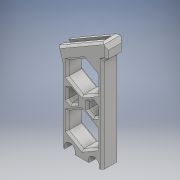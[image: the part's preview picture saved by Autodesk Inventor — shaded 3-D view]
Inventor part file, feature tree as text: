
AUTODESK INVENTOR PART (.ipt)
format: ipt  version: 2018 (Build 220112000, 112)  size: 381,440 bytes
history: native  units: mm
features: extrude x7, sketch x7, fillet x2, plane x1, chamfer x1, projected_geometry x1
ambient origin geometry x8: Origin, YZ Plane, XZ Plane, XY Plane, X Axis, Y Axis, Z Axis, Center Point
bodies: Solid1 (feature_tree)
feature tree (19):
  extrude  "Extrusion1"  Depth=70.0mm
  extrude  "Extrusion2"  Depth=10.0mm
  extrude  "Extrusion3"  TaperAngle=30.0deg  [1 undecoded]
  sketch  "Sketch7"  dims[d12=60.0deg d13=4.0mm d14=5.0mm d15=5.0mm]
  extrude  "Extrusion7"  Depth=5.0mm
  extrude  "Extrusion4"  Depth=7.0mm
  extrude  "Extrusion5"  Depth=4.0mm
  fillet  "Fillet1"  Radius=5.0mm
  fillet  "Fillet2"  Radius=5.0mm
  plane  "Work Plane1"
  extrude  "Extrusion9"  Depth=10.0mm
  chamfer  "Chamfer1"  Distance=15.0mm
  sketch  "Sketch1"  dims[d0=45.0mm d1=70.0mm]
  sketch  "Sketch2"  dims[d2=2.0mm d3=10.0mm]
  sketch  "Sketch3"  dims[d4=11.0mm d6=30.0deg]
  projected_geometry  "Projected Loop1"
  sketch  "Sketch5"  dims[d7=15.0mm d8=0.0mm d9=5.0mm]
  sketch  "Sketch6"  dims[d10=4.0mm d11=7.0mm]
  sketch  "Sketch11"  dims[d16=3.0mm d17=4.0mm d18=15.0mm d19=0.0mm d20=10.5mm d21=3.0mm d22=3.4mm d23=0.0mm d24=5.5mm d25=3.2mm d26=0.0mm d27=32.25mm d28=3.0mm d29=3.2mm d30=0.0mm d31=2.0mm d36=20.0mm d37=0.4mm d38=13.0mm d39=5.0mm d40=10.0mm d41=0.0mm d44=3.75mm d45=0.0mm d46=1.8mm d47=2.0mm d48=45.0deg]
note: 1 required parameter value undecoded (feature->parameter linkage not recoverable at this tier; creation-order binding heuristic only, values carry confidence <= 0.55)
